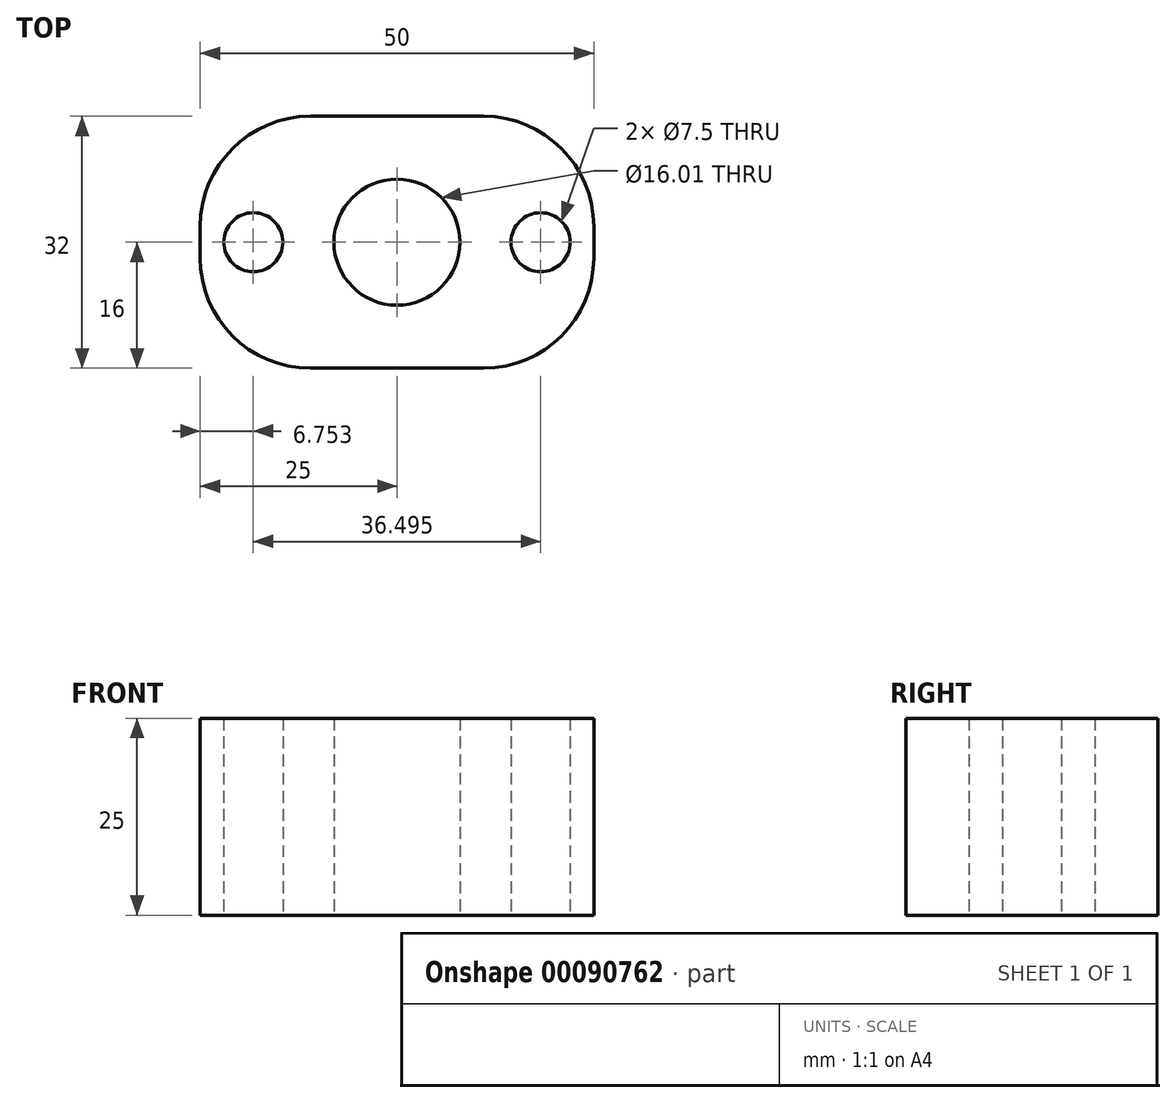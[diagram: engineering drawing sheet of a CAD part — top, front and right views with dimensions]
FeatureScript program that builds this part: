
annotation { "Feature Type Name" : "Feature", "Feature Type Description" : "" }
export const myFeature = defineFeature(function(context is Context, id is Id, definition is map)
    precondition{}
    {
        {
            var Q0;
            Q0=qCreatedBy(makeId("Top.planeOp"),FACE);
            var sketch = newSketch(context, id + "F0", { "sketchPlane" : qUnion([Q0])});
            skLineSegment(sketch, "E0.bottom", {"start": v(-11, 16) * mm, "end": v(11, 16) * mm});
            skLineSegment(sketch, "E0.top", {"start": v(-11, -16) * mm, "end": v(11, -16) * mm});
            skLineSegment(sketch, "E0.left", {"start": v(-25, 2) * mm, "end": v(-25, -2) * mm});
            skLineSegment(sketch, "E0.right", {"start": v(25, 2) * mm, "end": v(25, -2) * mm});
            skCircle(sketch, "E1", {"center": v(0, 0) * mm, "radius": 8 * mm});
            skCircle(sketch, "E2", {"center": v(-18.25, 0) * mm, "radius": 3.75 * mm});
            skCircle(sketch, "E3", {"center": v(18.25, 0) * mm, "radius": 3.75 * mm});
            skPoint(sketch, "E4.visualSharp", {"position": v(-25, 16) * mm});
            skArc(sketch, "E4.filletArc", {"start": v(-11, 16) * mm, "mid": v(-20.9, 11.9) * mm, "end": v(-25, 2) * mm});
            skPoint(sketch, "E5.visualSharp", {"position": v(25, 16) * mm});
            skArc(sketch, "E5.filletArc", {"start": v(25, 2) * mm, "mid": v(20.9, 11.9) * mm, "end": v(11, 16) * mm});
            skPoint(sketch, "E6.visualSharp", {"position": v(25, -16) * mm});
            skArc(sketch, "E6.filletArc", {"start": v(11, -16) * mm, "mid": v(20.9, -11.9) * mm, "end": v(25, -2) * mm});
            skPoint(sketch, "E7.visualSharp", {"position": v(-25, -16) * mm});
            skArc(sketch, "E7.filletArc", {"start": v(-25, -2) * mm, "mid": v(-20.9, -11.9) * mm, "end": v(-11, -16) * mm});
            skSolve(sketch);
        }
        {
            var Q0;
            Q0=makeQuery(id+"F0.imprint","IMPRINT",FACE,{"disambiguationData":[TD([[makeQuery(id+"F0.imprint","IMPRINT",EDGE,{"derivedFrom":sQuery(id+"F0.wireOp",EDGE,"E0.bottom")}),-1.0]])]});
            extrude(context, id + "F1", {"entities" : qUnion([Q0]), "depth" : 25 * mm});
        }
    });
